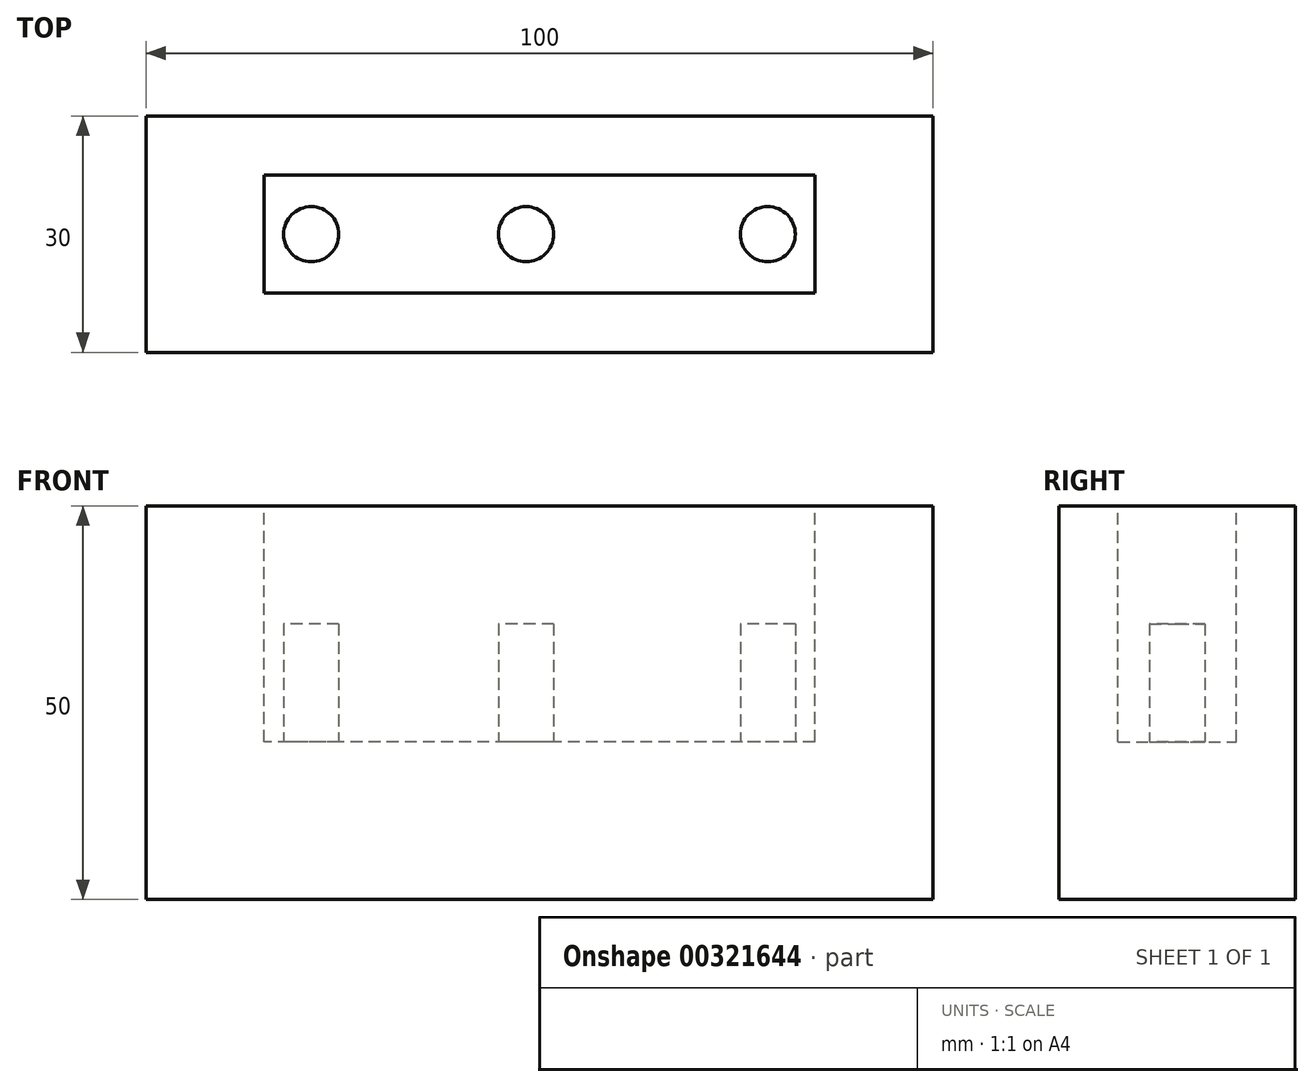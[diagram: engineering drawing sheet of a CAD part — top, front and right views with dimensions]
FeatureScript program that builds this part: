
annotation { "Feature Type Name" : "Feature", "Feature Type Description" : "" }
export const myFeature = defineFeature(function(context is Context, id is Id, definition is map)
    precondition{}
    {
        {
            var Q0;
            Q0=qCreatedBy(makeId("Top.planeOp"),FACE);
            var sketch = newSketch(context, id + "F0", { "sketchPlane" : qUnion([Q0])});
            skLineSegment(sketch, "E0.bottom", {"start": v(50, -15) * mm, "end": v(-50, -15) * mm});
            skLineSegment(sketch, "E0.top", {"start": v(50, 15) * mm, "end": v(-50, 15) * mm});
            skLineSegment(sketch, "E0.left", {"start": v(50, -15) * mm, "end": v(50, 15) * mm});
            skLineSegment(sketch, "E0.right", {"start": v(-50, -15) * mm, "end": v(-50, 15) * mm});
            skPoint(sketch, "E0.middle", {"position": v(0, 0) * mm});
            skSolve(sketch);
        }
        {
            var Q0;
            Q0=makeQuery(id+"F0.imprint","IMPRINT",FACE,{"disambiguationData":[TD([[makeQuery(id+"F0.imprint","IMPRINT",EDGE,{"derivedFrom":sQuery(id+"F0.wireOp",EDGE,"E0.bottom")}),-1.0]])]});
            extrude(context, id + "F1", {"entities" : qUnion([Q0]), "depth" : 50 * mm});
        }
        {
            var Q0;
            Q0=makeQuery(id+"F1.opExtrude","CAP_FACE",FACE,{"disambiguationData":[OSD([sQuery(id+"F0.wireOp",EDGE,"E0.bottom"),sQuery(id+"F0.wireOp",EDGE,"E0.top"),sQuery(id+"F0.wireOp",EDGE,"E0.left"),sQuery(id+"F0.wireOp",EDGE,"E0.right")])],"isStart":false});
            var sketch = newSketch(context, id + "F2", { "sketchPlane" : qUnion([Q0])});
            skLineSegment(sketch, "E1.bottom", {"start": v(35, -7.5) * mm, "end": v(-35, -7.5) * mm});
            skLineSegment(sketch, "E1.top", {"start": v(35, 7.5) * mm, "end": v(-35, 7.5) * mm});
            skLineSegment(sketch, "E1.left", {"start": v(35, -7.5) * mm, "end": v(35, 7.5) * mm});
            skLineSegment(sketch, "E1.right", {"start": v(-35, -7.5) * mm, "end": v(-35, 7.5) * mm});
            skPoint(sketch, "E1.middle", {"position": v(0, 0) * mm});
            skSolve(sketch);
        }
        {
            var Q0;
            Q0 = qSketchRegion(id + "F2", true);
            extrude(context, id + "F3", {"entities" : qUnion([Q0]), "operationType" : NewBodyOperationType.REMOVE, "oppositeDirection" : true, "depth" : 30 * mm});
        }
        {
            var Q0;
            Q0=makeQuery(id+"F3.boolean.opBoolean","COPY",FACE,{"derivedFrom":makeQuery(id+"F3.opExtrude","CAP_FACE",FACE,{"disambiguationData":[OSD([sQuery(id+"F2.wireOp",EDGE,"E1.bottom"),sQuery(id+"F2.wireOp",EDGE,"E1.top"),sQuery(id+"F2.wireOp",EDGE,"E1.left"),sQuery(id+"F2.wireOp",EDGE,"E1.right")])],"isStart":false})});
            var sketch = newSketch(context, id + "F4", { "sketchPlane" : qUnion([Q0])});
            skCircle(sketch, "E2", {"center": v(-1.71, 0) * mm, "radius": 3.5 * mm});
            skPoint(sketch, "E3.endSnap0", {"position": v(-35, 0) * mm});
            skPoint(sketch, "E4.endSnap0", {"position": v(35, 0) * mm});
            skCircle(sketch, "E5", {"center": v(-29, 0) * mm, "radius": 3.5 * mm});
            skCircle(sketch, "E6", {"center": v(29, 0) * mm, "radius": 3.5 * mm});
            skSolve(sketch);
        }
        {
            var Q0;
            Q0=makeQuery(id+"F4.imprint","IMPRINT",FACE,{"disambiguationData":[TD([[makeQuery(id+"F4.imprint","IMPRINT",EDGE,{"derivedFrom":sQuery(id+"F4.wireOp",EDGE,"E2")}),1.0]])]});
            var Q1;
            Q1=makeQuery(id+"F4.imprint","IMPRINT",FACE,{"disambiguationData":[TD([[makeQuery(id+"F4.imprint","IMPRINT",EDGE,{"derivedFrom":sQuery(id+"F4.wireOp",EDGE,"E6")}),1.0]])]});
            var Q2;
            Q2=makeQuery(id+"F4.imprint","IMPRINT",FACE,{"disambiguationData":[TD([[makeQuery(id+"F4.imprint","IMPRINT",EDGE,{"derivedFrom":sQuery(id+"F4.wireOp",EDGE,"E5")}),1.0]])]});
            extrude(context, id + "F5", {"entities" : qUnion([Q0, Q1, Q2]), "operationType" : NewBodyOperationType.ADD, "depth" : 15 * mm});
        }
    });
